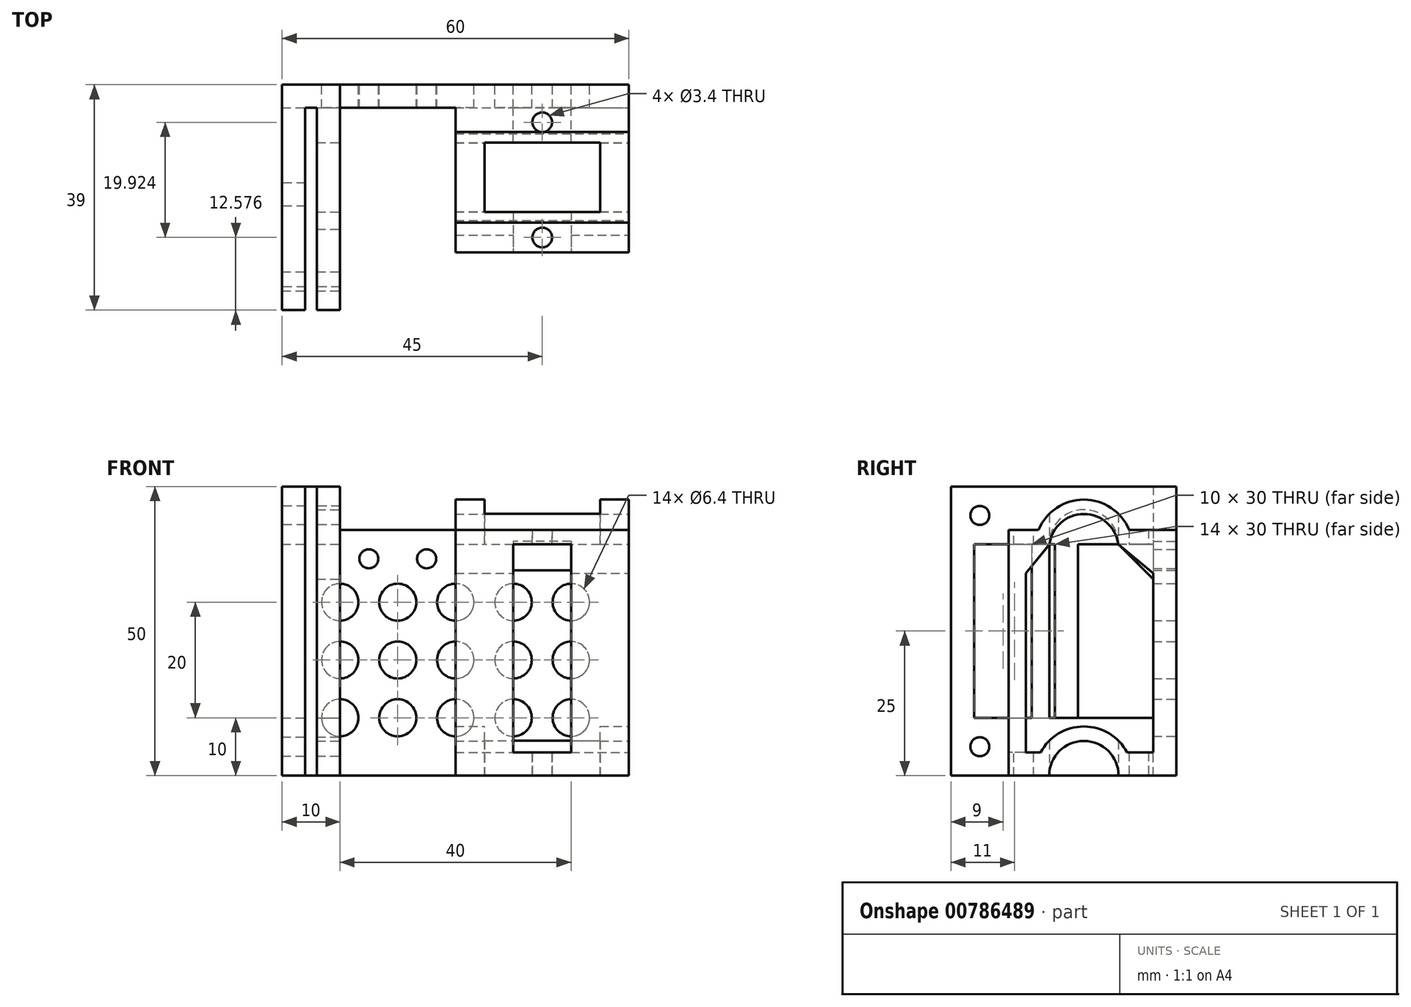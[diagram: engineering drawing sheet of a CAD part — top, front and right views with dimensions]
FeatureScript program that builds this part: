
annotation { "Feature Type Name" : "Feature", "Feature Type Description" : "" }
export const myFeature = defineFeature(function(context is Context, id is Id, definition is map)
    precondition{}
    {
        {
            var Q0;
            Q0=qCreatedBy(makeId("Front.planeOp"),FACE);
            var sketch = newSketch(context, id + "F0", { "sketchPlane" : qUnion([Q0])});
            skLineSegment(sketch, "E0.bottom", {"start": v(-30, 20) * mm, "end": v(30, 20) * mm});
            skLineSegment(sketch, "E0.top", {"start": v(-30, -20) * mm, "end": v(30, -20) * mm});
            skLineSegment(sketch, "E0.left", {"start": v(-30, 20) * mm, "end": v(-30, -20) * mm});
            skLineSegment(sketch, "E0.right", {"start": v(30, 20) * mm, "end": v(30, -20) * mm});
            skSolve(sketch);
        }
        {
            var Q0;
            Q0 = qSketchRegion(id + "F0", true);
            extrude(context, id + "F1", {"entities" : qUnion([Q0]), "depth" : 4 * mm, "offsetDistance" : 25 * mm});
        }
        {
            var Q0;
            Q0=makeQuery(id+"F1.opExtrude","CAP_FACE",FACE,{"disambiguationData":[OSD([sQuery(id+"F0.wireOp",EDGE,"E0.bottom"),sQuery(id+"F0.wireOp",EDGE,"E0.top"),sQuery(id+"F0.wireOp",EDGE,"E0.left"),sQuery(id+"F0.wireOp",EDGE,"E0.right")])],"isStart":false});
            var sketch = newSketch(context, id + "F2", { "sketchPlane" : qUnion([Q0])});
            skLineSegment(sketch, "E1.bottom", {"start": v(30, -20) * mm, "end": v(0, -20) * mm});
            skLineSegment(sketch, "E1.top", {"start": v(30, -10) * mm, "end": v(0, -10) * mm});
            skLineSegment(sketch, "E1.left", {"start": v(30, -20) * mm, "end": v(30, -10) * mm});
            skLineSegment(sketch, "E1.right", {"start": v(0, -20) * mm, "end": v(0, -10) * mm});
            skSolve(sketch);
        }
        {
            var Q0;
            Q0 = qSketchRegion(id + "F2", true);
            extrude(context, id + "F3", {"entities" : qUnion([Q0]), "operationType" : NewBodyOperationType.ADD, "depth" : 25 * mm, "offsetDistance" : 25 * mm});
        }
        {
            var Q0;
            Q0=makeQuery(id+"F1.opExtrude","CAP_FACE",FACE,{"disambiguationData":[OSD([sQuery(id+"F0.wireOp",EDGE,"E0.bottom"),sQuery(id+"F0.wireOp",EDGE,"E0.top"),sQuery(id+"F0.wireOp",EDGE,"E0.left"),sQuery(id+"F0.wireOp",EDGE,"E0.right")])],"isStart":false});
            var sketch = newSketch(context, id + "F4", { "sketchPlane" : qUnion([Q0])});
            skLineSegment(sketch, "E2.bottom", {"start": v(-30, -20) * mm, "end": v(-20, -20) * mm});
            skLineSegment(sketch, "E2.top", {"start": v(-30, -10) * mm, "end": v(-20, -10) * mm});
            skLineSegment(sketch, "E2.left", {"start": v(-30, -20) * mm, "end": v(-30, -10) * mm});
            skLineSegment(sketch, "E2.right", {"start": v(-20, -20) * mm, "end": v(-20, -10) * mm});
            skLineSegment(sketch, "E3.bottom", {"start": v(-17, -20) * mm, "end": v(-7, -20) * mm});
            skLineSegment(sketch, "E3.top", {"start": v(-17, 20) * mm, "end": v(-7, 20) * mm});
            skLineSegment(sketch, "E3.left", {"start": v(-17, -20) * mm, "end": v(-17, 20) * mm});
            skLineSegment(sketch, "E3.right", {"start": v(-7, -20) * mm, "end": v(-7, 20) * mm});
            skLineSegment(sketch, "E4.bottom", {"start": v(0, -15) * mm, "end": v(-4, -15) * mm});
            skLineSegment(sketch, "E4.top", {"start": v(0, -20) * mm, "end": v(-4, -20) * mm});
            skLineSegment(sketch, "E4.left", {"start": v(0, -15) * mm, "end": v(0, -20) * mm});
            skLineSegment(sketch, "E4.right", {"start": v(-4, -15) * mm, "end": v(-4, -20) * mm});
            skLineSegment(sketch, "E5.bottom", {"start": v(-26, -10) * mm, "end": v(-24, -10) * mm});
            skLineSegment(sketch, "E5.top", {"start": v(-26, -20) * mm, "end": v(-24, -20) * mm});
            skLineSegment(sketch, "E5.left", {"start": v(-26, -10) * mm, "end": v(-26, -20) * mm});
            skLineSegment(sketch, "E5.right", {"start": v(-24, -10) * mm, "end": v(-24, -20) * mm});
            skSolve(sketch);
        }
        {
            var Q0;
            {var subQ0=sQuery(id+"F4.wireOp",EDGE,"E2.left");Q0=makeQuery(id+"F4.imprint","IMPRINT",FACE,{"disambiguationData":[TD([[makeQuery(id+"F4.imprint","IMPRINT",EDGE,{"derivedFrom":subQ0}),1.0]])]});}
            var Q1;
            {var subQ0=sQuery(id+"F4.wireOp",EDGE,"E2.right");Q1=makeQuery(id+"F4.imprint","IMPRINT",FACE,{"disambiguationData":[TD([[makeQuery(id+"F4.imprint","IMPRINT",EDGE,{"derivedFrom":subQ0}),1.0]])]});}
            var Q2;
            Q2=makeQuery(id+"F4.imprint","IMPRINT",FACE,{"disambiguationData":[TD([[makeQuery(id+"F4.imprint","IMPRINT",EDGE,{"derivedFrom":sQuery(id+"F4.wireOp",EDGE,"E3.bottom")}),1.0]])]});
            extrude(context, id + "F5", {"entities" : qUnion([Q0, Q1, Q2]), "operationType" : NewBodyOperationType.ADD, "depth" : 25 * mm, "offsetDistance" : 25 * mm});
        }
        {
            var Q0;
            Q0=makeQuery(id+"F3.boolean.opBoolean","MERGE",FACE,{"derivedFrom":[makeQuery(id+"F1.opExtrude","SWEPT_FACE",FACE,{"disambiguationData":[OSD([sQuery(id+"F0.wireOp",EDGE,"E0.right")])]}),makeQuery(id+"F3.opExtrude","SWEPT_FACE",FACE,{"disambiguationData":[OSD([sQuery(id+"F2.wireOp",EDGE,"E1.left")])]})]});
            var sketch = newSketch(context, id + "F6", { "sketchPlane" : qUnion([Q0])});
            skCircle(sketch, "E6", {"center": v(-16.5, -20) * mm, "radius": 0.15 * mm});
            skLineSegment(sketch, "E7", {"start": v(-29, -10) * mm, "end": v(-16.5, -10) * mm});
            skSolve(sketch);
        }
        {
            var Q0;
            Q0=makeQuery(id+"F5.opExtrude","SWEPT_FACE",FACE,{"disambiguationData":[OSD([sQuery(id+"F4.wireOp",EDGE,"E2.right")])]});
            var sketch = newSketch(context, id + "F7", { "sketchPlane" : qUnion([Q0])});
            skCircle(sketch, "E8", {"center": v(-16, -20) * mm, "radius": 6 * mm});
            skSolve(sketch);
        }
        {
            var Q0;
            Q0 = qSketchRegion(id + "F7", true);
            extrude(context, id + "F8", {"entities" : qUnion([Q0]), "operationType" : NewBodyOperationType.REMOVE, "oppositeDirection" : true, "depth" : 4 * mm, "offsetDistance" : 25 * mm});
        }
        {
            var Q0;
            Q0=makeQuery(id+"F5.opExtrude","CAP_FACE",FACE,{"disambiguationData":[OSD([sQuery(id+"F4.wireOp",EDGE,"E2.bottom"),sQuery(id+"F4.wireOp",EDGE,"E2.top"),sQuery(id+"F4.wireOp",EDGE,"E2.right"),sQuery(id+"F4.wireOp",EDGE,"E5.right")])],"isStart":false});
            var sketch = newSketch(context, id + "F9", { "sketchPlane" : qUnion([Q0])});
            skLineSegment(sketch, "E9.bottom", {"start": v(-24, -10) * mm, "end": v(-20, -10) * mm});
            skLineSegment(sketch, "E9.top", {"start": v(-24, -20) * mm, "end": v(-20, -20) * mm});
            skLineSegment(sketch, "E9.left", {"start": v(-24, -10) * mm, "end": v(-24, -20) * mm});
            skLineSegment(sketch, "E9.right", {"start": v(-20, -10) * mm, "end": v(-20, -20) * mm});
            skSolve(sketch);
        }
        {
            var Q0;
            Q0 = qSketchRegion(id + "F9", true);
            extrude(context, id + "F10", {"entities" : qUnion([Q0]), "operationType" : NewBodyOperationType.ADD, "depth" : 10 * mm, "offsetDistance" : 25 * mm});
        }
        {
            var Q0;
            Q0=makeQuery(id+"F5.opExtrude","CAP_FACE",FACE,{"disambiguationData":[OSD([sQuery(id+"F4.wireOp",EDGE,"E2.bottom"),sQuery(id+"F4.wireOp",EDGE,"E2.top"),sQuery(id+"F4.wireOp",EDGE,"E2.left"),sQuery(id+"F4.wireOp",EDGE,"E5.left")])],"isStart":false});
            var sketch = newSketch(context, id + "F11", { "sketchPlane" : qUnion([Q0])});
            skLineSegment(sketch, "E10.bottom", {"start": v(-30, -10) * mm, "end": v(-26, -10) * mm});
            skLineSegment(sketch, "E10.top", {"start": v(-30, -20) * mm, "end": v(-26, -20) * mm});
            skLineSegment(sketch, "E10.left", {"start": v(-30, -10) * mm, "end": v(-30, -20) * mm});
            skLineSegment(sketch, "E10.right", {"start": v(-26, -10) * mm, "end": v(-26, -20) * mm});
            skSolve(sketch);
        }
        {
            var Q0;
            Q0 = qSketchRegion(id + "F11", true);
            extrude(context, id + "F12", {"entities" : qUnion([Q0]), "operationType" : NewBodyOperationType.ADD, "depth" : 10 * mm, "offsetDistance" : 25 * mm});
        }
        {
            var Q0;
            Q0=makeQuery(id+"F10.boolean.opBoolean","MERGE",FACE,{"derivedFrom":[makeQuery(id+"F5.opExtrude","SWEPT_FACE",FACE,{"disambiguationData":[OSD([sQuery(id+"F4.wireOp",EDGE,"E2.right")])]}),makeQuery(id+"F10.opExtrude","SWEPT_FACE",FACE,{"disambiguationData":[OSD([sQuery(id+"F9.wireOp",EDGE,"E9.right")])]})]});
            var sketch = newSketch(context, id + "F13", { "sketchPlane" : qUnion([Q0])});
            skCircle(sketch, "E11", {"center": v(-34, -15) * mm, "radius": 1.65 * mm});
            skPoint(sketch, "E11.centerSnap0", {"position": v(-39, -15) * mm});
            skSolve(sketch);
        }
        {
            var Q0;
            Q0 = qSketchRegion(id + "F13", true);
            extrude(context, id + "F14", {"entities" : qUnion([Q0]), "operationType" : NewBodyOperationType.REMOVE, "oppositeDirection" : true, "depth" : 25 * mm, "offsetDistance" : 25 * mm});
        }
        {
            var Q0;
            Q0=makeQuery(id+"F5.boolean.opBoolean","MERGE",FACE,{"derivedFrom":[makeQuery(id+"F1.opExtrude","SWEPT_FACE",FACE,{"disambiguationData":[OSD([sQuery(id+"F0.wireOp",EDGE,"E0.bottom")])]}),makeQuery(id+"F5.opExtrude","SWEPT_FACE",FACE,{"disambiguationData":[OSD([sQuery(id+"F4.wireOp",EDGE,"E3.top")])]})]});
            extrude(context, id + "F15", {"entities" : qUnion([Q0]), "operationType" : NewBodyOperationType.ADD, "depth" : 10 * mm, "offsetDistance" : 25 * mm});
        }
        {
            var Q0;
            {var subQ0=sQuery(id+"F7yCQw9h8FRDPHP_1.wireOp",EDGE,"DOwKe9Eh-Jl7f-Skud-Ed76-K8RTFp9YU4bL");var subQ1=sQuery(id+"F0.wireOp",EDGE,"E0.bottom");var subQ7=sQuery(id+"F0.wireOp",EDGE,"E0.top");var subQ14=sQuery(id+"F0.wireOp",EDGE,"E0.left");var subQ19=sQuery(id+"F0.wireOp",EDGE,"E0.right");var subQ20=makeQuery(id+"F1.opExtrude","CAP_FACE",FACE,{"disambiguationData":[OSD([subQ1,subQ7,subQ14,subQ19])],"isStart":false});Q0=makeQuery(id+"F15.boolean.opBoolean","MERGE",FACE,{"derivedFrom":[makeQuery(id+"FMx2agXSYsnFbtv_1.boolean.opBoolean","MERGE",FACE,{"derivedFrom":[makeQuery(id+"F5.boolean.opBoolean","SPLIT",FACE,{"disambiguationData":[TD([makeQuery(id+"F1.opExtrude","SWEPT_FACE",FACE,{"disambiguationData":[OSD([subQ19])]})])],"derivedFrom":subQ20}),makeQuery(id+"F5.boolean.opBoolean","SPLIT",FACE,{"disambiguationData":[TD([makeQuery(id+"F1.opExtrude","SWEPT_FACE",FACE,{"disambiguationData":[OSD([subQ14])]})])],"derivedFrom":subQ20}),makeQuery(id+"FMx2agXSYsnFbtv_1.opExtrude","SWEPT_FACE",FACE,{"disambiguationData":[OSD([subQ0])]})]}),makeQuery(id+"F15.opExtrude","SWEPT_FACE",FACE,{"disambiguationData":[OSD([subQ1,subQ0])]})]});}
            var sketch = newSketch(context, id + "F16", { "sketchPlane" : qUnion([Q0])});
            skLineSegment(sketch, "E12.bottom", {"start": v(-30, 30) * mm, "end": v(-26, 30) * mm});
            skLineSegment(sketch, "E12.top", {"start": v(-30, 20) * mm, "end": v(-26, 20) * mm});
            skLineSegment(sketch, "E12.left", {"start": v(-30, 30) * mm, "end": v(-30, 20) * mm});
            skLineSegment(sketch, "E12.right", {"start": v(-26, 30) * mm, "end": v(-26, 20) * mm});
            skLineSegment(sketch, "E13.bottom", {"start": v(-24, 30) * mm, "end": v(-20, 30) * mm});
            skLineSegment(sketch, "E13.top", {"start": v(-24, 20) * mm, "end": v(-20, 20) * mm});
            skLineSegment(sketch, "E13.left", {"start": v(-24, 30) * mm, "end": v(-24, 20) * mm});
            skLineSegment(sketch, "E13.right", {"start": v(-20, 30) * mm, "end": v(-20, 20) * mm});
            skSolve(sketch);
        }
        {
            var Q0;
            Q0 = qSketchRegion(id + "F16", true);
            extrude(context, id + "F17", {"entities" : qUnion([Q0]), "operationType" : NewBodyOperationType.ADD, "depth" : 35 * mm, "offsetDistance" : 25 * mm});
        }
        {
            var Q0;
            Q0=makeQuery(id+"F17.opExtrude","SWEPT_FACE",FACE,{"disambiguationData":[OSD([sQuery(id+"F16.wireOp",EDGE,"E13.right")])]});
            var sketch = newSketch(context, id + "F18", { "sketchPlane" : qUnion([Q0])});
            skCircle(sketch, "E14", {"center": v(-16, 20) * mm, "radius": 6 * mm});
            skSolve(sketch);
        }
        {
            var Q0;
            Q0 = qSketchRegion(id + "F18", true);
            extrude(context, id + "F19", {"entities" : qUnion([Q0]), "operationType" : NewBodyOperationType.REMOVE, "oppositeDirection" : true, "depth" : 4 * mm, "offsetDistance" : 25 * mm});
        }
        {
            var Q0;
            Q0 = qSketchRegion(id + "F7", true);
            extrude(context, id + "F20", {"entities" : qUnion([Q0]), "operationType" : NewBodyOperationType.REMOVE, "oppositeDirection" : true, "depth" : 4 * mm, "offsetDistance" : 25 * mm});
        }
        {
            var Q0;
            {var subQ0=sQuery(id+"F0.wireOp",EDGE,"E0.left");Q0=makeQuery(id+"F17.boolean.opBoolean","MERGE",FACE,{"derivedFrom":[makeQuery(id+"F15.boolean.opBoolean","MERGE",FACE,{"derivedFrom":[makeQuery(id+"F12.boolean.opBoolean","MERGE",FACE,{"derivedFrom":[makeQuery(id+"F5.boolean.opBoolean","MERGE",FACE,{"derivedFrom":[makeQuery(id+"F1.opExtrude","SWEPT_FACE",FACE,{"disambiguationData":[OSD([subQ0])]}),makeQuery(id+"F5.opExtrude","SWEPT_FACE",FACE,{"disambiguationData":[OSD([sQuery(id+"F4.wireOp",EDGE,"E2.left")])]})]}),makeQuery(id+"F12.opExtrude","SWEPT_FACE",FACE,{"disambiguationData":[OSD([sQuery(id+"F11.wireOp",EDGE,"E10.left")])]})]}),makeQuery(id+"F15.opExtrude","SWEPT_FACE",FACE,{"disambiguationData":[OSD([sQuery(id+"F0.wireOp",EDGE,"E0.bottom"),subQ0])]})]}),makeQuery(id+"F17.opExtrude","SWEPT_FACE",FACE,{"disambiguationData":[OSD([sQuery(id+"F16.wireOp",EDGE,"E12.left")])]})]});}
            var sketch = newSketch(context, id + "F21", { "sketchPlane" : qUnion([Q0])});
            skCircle(sketch, "E15", {"center": v(34, 25) * mm, "radius": 1.65 * mm});
            skSolve(sketch);
        }
        {
            var Q0;
            Q0 = qSketchRegion(id + "F21", true);
            extrude(context, id + "F22", {"entities" : qUnion([Q0]), "operationType" : NewBodyOperationType.REMOVE, "oppositeDirection" : true, "depth" : 10 * mm, "offsetDistance" : 25 * mm});
        }
        {
            var Q0;
            {var subQ0=sQuery(id+"F7yCQw9h8FRDPHP_1.wireOp",EDGE,"DOwKe9Eh-Jl7f-Skud-Ed76-K8RTFp9YU4bL");var subQ1=sQuery(id+"F0.wireOp",EDGE,"E0.bottom");var subQ7=sQuery(id+"F0.wireOp",EDGE,"E0.top");var subQ14=sQuery(id+"F0.wireOp",EDGE,"E0.left");var subQ19=sQuery(id+"F0.wireOp",EDGE,"E0.right");var subQ20=makeQuery(id+"F1.opExtrude","CAP_FACE",FACE,{"disambiguationData":[OSD([subQ1,subQ7,subQ14,subQ19])],"isStart":false});Q0=makeQuery(id+"F15.boolean.opBoolean","MERGE",FACE,{"derivedFrom":[makeQuery(id+"FMx2agXSYsnFbtv_1.boolean.opBoolean","MERGE",FACE,{"derivedFrom":[makeQuery(id+"F5.boolean.opBoolean","SPLIT",FACE,{"disambiguationData":[TD([makeQuery(id+"F1.opExtrude","SWEPT_FACE",FACE,{"disambiguationData":[OSD([subQ19])]})])],"derivedFrom":subQ20}),makeQuery(id+"F5.boolean.opBoolean","SPLIT",FACE,{"disambiguationData":[TD([makeQuery(id+"F1.opExtrude","SWEPT_FACE",FACE,{"disambiguationData":[OSD([subQ14])]})])],"derivedFrom":subQ20}),makeQuery(id+"FMx2agXSYsnFbtv_1.opExtrude","SWEPT_FACE",FACE,{"disambiguationData":[OSD([subQ0])]})]}),makeQuery(id+"F15.opExtrude","SWEPT_FACE",FACE,{"disambiguationData":[OSD([subQ1,subQ0])]})]});}
            var sketch = newSketch(context, id + "F23", { "sketchPlane" : qUnion([Q0])});
            skLineSegment(sketch, "E16.bottom", {"start": v(30, 30) * mm, "end": v(0, 30) * mm});
            skLineSegment(sketch, "E16.top", {"start": v(30, 20) * mm, "end": v(0, 20) * mm});
            skLineSegment(sketch, "E16.left", {"start": v(30, 30) * mm, "end": v(30, 20) * mm});
            skLineSegment(sketch, "E16.right", {"start": v(0, 30) * mm, "end": v(0, 20) * mm});
            skSolve(sketch);
        }
        {
            var Q0;
            Q0 = qSketchRegion(id + "F23", true);
            extrude(context, id + "F24", {"entities" : qUnion([Q0]), "operationType" : NewBodyOperationType.ADD, "depth" : 25 * mm, "offsetDistance" : 25 * mm});
        }
        {
            var Q0;
            {var subQ0=sQuery(id+"F4.wireOp",EDGE,"E2.top");Q0=makeQuery(id+"F12.boolean.opBoolean","MERGE",FACE,{"derivedFrom":[makeQuery(id+"F5.opExtrude","SWEPT_FACE",FACE,{"disambiguationData":[OSD([subQ0]),TDD([makeQuery(id+"F4.imprint","IMPRINT",EDGE,{"disambiguationData":[TD([[makeQuery(id+"F4.imprint","INTERSECT",VERTEX,{"derivedFrom":[subQ0,sQuery(id+"F4.wireOp",EDGE,"E5.left")]}),1.0]])],"derivedFrom":subQ0})])]}),makeQuery(id+"F12.opExtrude","SWEPT_FACE",FACE,{"disambiguationData":[OSD([sQuery(id+"F11.wireOp",EDGE,"E10.bottom")])]})]});}
            var sketch = newSketch(context, id + "F25", { "sketchPlane" : qUnion([Q0])});
            skLineSegment(sketch, "E17.bottom", {"start": v(-20, -39) * mm, "end": v(-24, -39) * mm});
            skLineSegment(sketch, "E17.top", {"start": v(-20, -35) * mm, "end": v(-24, -35) * mm});
            skLineSegment(sketch, "E17.left", {"start": v(-20, -39) * mm, "end": v(-20, -35) * mm});
            skLineSegment(sketch, "E17.right", {"start": v(-24, -39) * mm, "end": v(-24, -35) * mm});
            skLineSegment(sketch, "E18.bottom", {"start": v(-26, -39) * mm, "end": v(-30, -39) * mm});
            skLineSegment(sketch, "E18.top", {"start": v(-26, -35) * mm, "end": v(-30, -35) * mm});
            skLineSegment(sketch, "E18.left", {"start": v(-26, -39) * mm, "end": v(-26, -35) * mm});
            skLineSegment(sketch, "E18.right", {"start": v(-30, -39) * mm, "end": v(-30, -35) * mm});
            skSolve(sketch);
        }
        {
            var Q0;
            Q0 = qSketchRegion(id + "F25", true);
            extrude(context, id + "F26", {"entities" : qUnion([Q0]), "operationType" : NewBodyOperationType.ADD, "depth" : 30 * mm, "offsetDistance" : 25 * mm});
        }
        {
            var Q0;
            Q0=makeQuery(id+"F26.boolean.opBoolean","MERGE",FACE,{"derivedFrom":[makeQuery(id+"F10.boolean.opBoolean","MERGE",FACE,{"derivedFrom":[makeQuery(id+"F5.opExtrude","SWEPT_FACE",FACE,{"disambiguationData":[OSD([sQuery(id+"F4.wireOp",EDGE,"E2.right")])]}),makeQuery(id+"F10.opExtrude","SWEPT_FACE",FACE,{"disambiguationData":[OSD([sQuery(id+"F9.wireOp",EDGE,"E9.right")])]})]}),makeQuery(id+"F17.opExtrude","SWEPT_FACE",FACE,{"disambiguationData":[OSD([sQuery(id+"F16.wireOp",EDGE,"E13.right")])]}),makeQuery(id+"F26.opExtrude","SWEPT_FACE",FACE,{"disambiguationData":[OSD([sQuery(id+"F25.wireOp",EDGE,"E17.left")])]})]});
            var sketch = newSketch(context, id + "F27", { "sketchPlane" : qUnion([Q0])});
            skLineSegment(sketch, "E19.bottom", {"start": v(-22, 20) * mm, "end": v(-25, 20) * mm});
            skLineSegment(sketch, "E19.top", {"start": v(-22, -10) * mm, "end": v(-25, -10) * mm});
            skLineSegment(sketch, "E19.left", {"start": v(-22, 20) * mm, "end": v(-22, -10) * mm});
            skLineSegment(sketch, "E19.right", {"start": v(-25, 20) * mm, "end": v(-25, -10) * mm});
            skLineSegment(sketch, "E20", {"start": v(-10, 20) * mm, "end": v(-4, 14) * mm});
            skLineSegment(sketch, "E21", {"start": v(-10, 20) * mm, "end": v(-4, 20) * mm});
            skLineSegment(sketch, "E22", {"start": v(-4, 20) * mm, "end": v(-4, 14) * mm});
            skSolve(sketch);
        }
        {
            var Q0;
            Q0 = qSketchRegion(id + "F27", true);
            extrude(context, id + "F28", {"entities" : qUnion([Q0]), "operationType" : NewBodyOperationType.ADD, "oppositeDirection" : true, "depth" : 4 * mm, "offsetDistance" : 25 * mm});
        }
        {
            var Q0;
            {var subQ0=sQuery(id+"F0.wireOp",EDGE,"E0.left");Q0=makeQuery(id+"F26.boolean.opBoolean","MERGE",FACE,{"derivedFrom":[makeQuery(id+"F17.boolean.opBoolean","MERGE",FACE,{"derivedFrom":[makeQuery(id+"F15.boolean.opBoolean","MERGE",FACE,{"derivedFrom":[makeQuery(id+"F12.boolean.opBoolean","MERGE",FACE,{"derivedFrom":[makeQuery(id+"F5.boolean.opBoolean","MERGE",FACE,{"derivedFrom":[makeQuery(id+"F1.opExtrude","SWEPT_FACE",FACE,{"disambiguationData":[OSD([subQ0])]}),makeQuery(id+"F5.opExtrude","SWEPT_FACE",FACE,{"disambiguationData":[OSD([sQuery(id+"F4.wireOp",EDGE,"E2.left")])]})]}),makeQuery(id+"F12.opExtrude","SWEPT_FACE",FACE,{"disambiguationData":[OSD([sQuery(id+"F11.wireOp",EDGE,"E10.left")])]})]}),makeQuery(id+"F15.opExtrude","SWEPT_FACE",FACE,{"disambiguationData":[OSD([sQuery(id+"F0.wireOp",EDGE,"E0.bottom"),subQ0])]})]}),makeQuery(id+"F17.opExtrude","SWEPT_FACE",FACE,{"disambiguationData":[OSD([sQuery(id+"F16.wireOp",EDGE,"E12.left")])]})]}),makeQuery(id+"F26.opExtrude","SWEPT_FACE",FACE,{"disambiguationData":[OSD([sQuery(id+"F25.wireOp",EDGE,"E18.right")])]})]});}
            var sketch = newSketch(context, id + "F29", { "sketchPlane" : qUnion([Q0])});
            skLineSegment(sketch, "E23.bottom", {"start": v(17, 20) * mm, "end": v(21, 20) * mm});
            skLineSegment(sketch, "E23.top", {"start": v(17, -10) * mm, "end": v(21, -10) * mm});
            skLineSegment(sketch, "E23.left", {"start": v(17, 20) * mm, "end": v(17, -10) * mm});
            skLineSegment(sketch, "E23.right", {"start": v(21, 20) * mm, "end": v(21, -10) * mm});
            skSolve(sketch);
        }
        {
            var Q0;
            Q0 = qSketchRegion(id + "F29", true);
            extrude(context, id + "F30", {"entities" : qUnion([Q0]), "operationType" : NewBodyOperationType.ADD, "oppositeDirection" : true, "depth" : 4 * mm, "offsetDistance" : 25 * mm});
        }
        {
            var Q0;
            Q0=makeQuery(id+"F3.opExtrude","SWEPT_FACE",FACE,{"disambiguationData":[OSD([sQuery(id+"F2.wireOp",EDGE,"E1.top")])]});
            var sketch = newSketch(context, id + "F31", { "sketchPlane" : qUnion([Q0])});
            skLineSegment(sketch, "E24.bottom", {"start": v(0, -29) * mm, "end": v(30, -29) * mm});
            skLineSegment(sketch, "E24.top", {"start": v(0, -26) * mm, "end": v(30, -26) * mm});
            skLineSegment(sketch, "E24.left", {"start": v(0, -29) * mm, "end": v(0, -26) * mm});
            skLineSegment(sketch, "E24.right", {"start": v(30, -29) * mm, "end": v(30, -26) * mm});
            skSolve(sketch);
        }
        {
            var Q0;
            Q0 = qSketchRegion(id + "F31", true);
            extrude(context, id + "F32", {"entities" : qUnion([Q0]), "operationType" : NewBodyOperationType.ADD, "depth" : 30 * mm, "offsetDistance" : 25 * mm});
        }
        {
            var Q0;
            {var subQ0=sQuery(id+"F0.wireOp",EDGE,"E0.right");Q0=makeQuery(id+"F32.boolean.opBoolean","MERGE",FACE,{"derivedFrom":[makeQuery(id+"F24.boolean.opBoolean","MERGE",FACE,{"derivedFrom":[makeQuery(id+"F15.boolean.opBoolean","MERGE",FACE,{"derivedFrom":[makeQuery(id+"FrBbq9cCnRRpS4j_1.boolean.opBoolean","MERGE",FACE,{"derivedFrom":[makeQuery(id+"F3.boolean.opBoolean","MERGE",FACE,{"derivedFrom":[makeQuery(id+"F1.opExtrude","SWEPT_FACE",FACE,{"disambiguationData":[OSD([subQ0])]}),makeQuery(id+"F3.opExtrude","SWEPT_FACE",FACE,{"disambiguationData":[OSD([sQuery(id+"F2.wireOp",EDGE,"E1.left")])]})]}),makeQuery(id+"FrBbq9cCnRRpS4j_1.opExtrude","CAP_FACE",FACE,{"disambiguationData":[OSD([sQuery(id+"F6.wireOp",EDGE,"E6")])],"isStart":true})]}),makeQuery(id+"F15.opExtrude","SWEPT_FACE",FACE,{"disambiguationData":[OSD([sQuery(id+"F0.wireOp",EDGE,"E0.bottom"),subQ0])]})]}),makeQuery(id+"F24.opExtrude","SWEPT_FACE",FACE,{"disambiguationData":[OSD([sQuery(id+"F23.wireOp",EDGE,"E16.left")])]})]}),makeQuery(id+"F32.opExtrude","SWEPT_FACE",FACE,{"disambiguationData":[OSD([sQuery(id+"F31.wireOp",EDGE,"E24.right")])]})]});}
            var sketch = newSketch(context, id + "F33", { "sketchPlane" : qUnion([Q0])});
            skArc(sketch, "E25", {"start": v(-10.05, 20) * mm, "mid": v(-16, 25.24) * mm, "end": v(-21.95, 20) * mm});
            skArc(sketch, "E26", {"start": v(-7.53, 20) * mm, "mid": v(-16, 27.74) * mm, "end": v(-24.47, 20) * mm});
            skArc(sketch, "E27", {"start": v(-10, -20) * mm, "mid": v(-16, -14) * mm, "end": v(-22, -20) * mm});
            skArc(sketch, "E28", {"start": v(-7.5, -20) * mm, "mid": v(-16, -11.5) * mm, "end": v(-24.5, -20) * mm});
            skLineSegment(sketch, "E29", {"start": v(-22, -20) * mm, "end": v(-24.5, -20) * mm});
            skLineSegment(sketch, "E30", {"start": v(-10, -20) * mm, "end": v(-7.5, -20) * mm});
            skLineSegment(sketch, "E31", {"start": v(-24.47, 20) * mm, "end": v(-21.95, 20) * mm});
            skLineSegment(sketch, "E32", {"start": v(-10.05, 20) * mm, "end": v(-7.53, 20) * mm});
            skLineSegment(sketch, "E33", {"start": v(-29, 22.5) * mm, "end": v(-29, 30) * mm});
            skLineSegment(sketch, "E34", {"start": v(-29, 30) * mm, "end": v(-4.99, 30) * mm});
            skLineSegment(sketch, "E35", {"start": v(-23.85, 22.5) * mm, "end": v(-29, 22.5) * mm});
            skPoint(sketch, "E36.orphan", {"position": v(-29, 20) * mm});
            skLineSegment(sketch, "E37", {"start": v(-8.15, 22.5) * mm, "end": v(-4, 22.5) * mm});
            skLineSegment(sketch, "E38", {"start": v(-4, 22.5) * mm, "end": v(-4, 30) * mm});
            skLineSegment(sketch, "E39", {"start": v(-4, 30) * mm, "end": v(-4.99, 30) * mm});
            skLineSegment(sketch, "E40", {"start": v(-26, -10) * mm, "end": v(-26, -16) * mm});
            skLineSegment(sketch, "E41", {"start": v(-26, -16) * mm, "end": v(-23.5, -16) * mm});
            skLineSegment(sketch, "E42", {"start": v(-4, -10) * mm, "end": v(-4, -16) * mm});
            skLineSegment(sketch, "E43", {"start": v(-4, -16) * mm, "end": v(-8.5, -16) * mm});
            skSolve(sketch);
        }
        {
            var Q0;
            {var subQ0=sQuery(id+"F33.wireOp",EDGE,"E25");Q0=makeQuery(id+"F33.imprint","IMPRINT",FACE,{"disambiguationData":[TD([[makeQuery(id+"F33.imprint","IMPRINT",EDGE,{"derivedFrom":subQ0}),1.0]])]});}
            var Q1;
            {var subQ0=sQuery(id+"F33.wireOp",EDGE,"E27");Q1=makeQuery(id+"F33.imprint","IMPRINT",FACE,{"disambiguationData":[TD([[makeQuery(id+"F33.imprint","IMPRINT",EDGE,{"derivedFrom":subQ0}),1.0]])]});}
            extrude(context, id + "F34", {"entities" : qUnion([Q0, Q1]), "operationType" : NewBodyOperationType.REMOVE, "oppositeDirection" : true, "depth" : 30 * mm, "offsetDistance" : 25 * mm});
        }
        {
            var Q0;
            {var subQ0=sQuery(id+"F0.wireOp",EDGE,"E0.right");Q0=makeQuery(id+"F32.boolean.opBoolean","MERGE",FACE,{"derivedFrom":[makeQuery(id+"F24.boolean.opBoolean","MERGE",FACE,{"derivedFrom":[makeQuery(id+"F15.boolean.opBoolean","MERGE",FACE,{"derivedFrom":[makeQuery(id+"FrBbq9cCnRRpS4j_1.boolean.opBoolean","MERGE",FACE,{"derivedFrom":[makeQuery(id+"F3.boolean.opBoolean","MERGE",FACE,{"derivedFrom":[makeQuery(id+"F1.opExtrude","SWEPT_FACE",FACE,{"disambiguationData":[OSD([subQ0])]}),makeQuery(id+"F3.opExtrude","SWEPT_FACE",FACE,{"disambiguationData":[OSD([sQuery(id+"F2.wireOp",EDGE,"E1.left")])]})]}),makeQuery(id+"FrBbq9cCnRRpS4j_1.opExtrude","CAP_FACE",FACE,{"disambiguationData":[OSD([sQuery(id+"F6.wireOp",EDGE,"E6")])],"isStart":true})]}),makeQuery(id+"F15.opExtrude","SWEPT_FACE",FACE,{"disambiguationData":[OSD([sQuery(id+"F0.wireOp",EDGE,"E0.bottom"),subQ0])]})]}),makeQuery(id+"F24.opExtrude","SWEPT_FACE",FACE,{"disambiguationData":[OSD([sQuery(id+"F23.wireOp",EDGE,"E16.left")])]})]}),makeQuery(id+"F32.opExtrude","SWEPT_FACE",FACE,{"disambiguationData":[OSD([sQuery(id+"F31.wireOp",EDGE,"E24.right")])]})]});}
            var sketch = newSketch(context, id + "F35", { "sketchPlane" : qUnion([Q0])});
            skLineSegment(sketch, "E44", {"start": v(-21.95, 20) * mm, "end": v(-26, 15) * mm});
            skLineSegment(sketch, "E45", {"start": v(-21.95, 20) * mm, "end": v(-26, 20) * mm});
            skLineSegment(sketch, "E46", {"start": v(-26, 20) * mm, "end": v(-26, 15) * mm});
            skLineSegment(sketch, "E47", {"start": v(-10.05, 20) * mm, "end": v(-4, 15) * mm});
            skLineSegment(sketch, "E48", {"start": v(-4, 15) * mm, "end": v(-4, 20) * mm});
            skLineSegment(sketch, "E49", {"start": v(-4, 20) * mm, "end": v(-10.05, 20) * mm});
            skSolve(sketch);
        }
        {
            var Q0;
            Q0=makeQuery(id+"F35.imprint","IMPRINT",FACE,{"disambiguationData":[TD([[makeQuery(id+"F35.imprint","IMPRINT",EDGE,{"derivedFrom":sQuery(id+"F35.wireOp",EDGE,"E47")}),1.0]])]});
            var Q1;
            Q1=makeQuery(id+"F35.imprint","IMPRINT",FACE,{"disambiguationData":[TD([[makeQuery(id+"F35.imprint","IMPRINT",EDGE,{"derivedFrom":sQuery(id+"F35.wireOp",EDGE,"E44")}),-1.0]])]});
            extrude(context, id + "F36", {"entities" : qUnion([Q0, Q1]), "operationType" : NewBodyOperationType.ADD, "oppositeDirection" : true, "depth" : 30 * mm, "offsetDistance" : 25 * mm});
        }
        {
            var Q0;
            Q0=makeQuery(id+"F32.boolean.opBoolean","MERGE",FACE,{"derivedFrom":[makeQuery(id+"F3.opExtrude","CAP_FACE",FACE,{"disambiguationData":[OSD([sQuery(id+"F2.wireOp",EDGE,"E1.bottom"),sQuery(id+"F2.wireOp",EDGE,"E1.top"),sQuery(id+"F2.wireOp",EDGE,"E1.left"),sQuery(id+"F2.wireOp",EDGE,"E1.right")])],"isStart":false}),makeQuery(id+"F24.opExtrude","CAP_FACE",FACE,{"disambiguationData":[OSD([sQuery(id+"F23.wireOp",EDGE,"E16.bottom"),sQuery(id+"F23.wireOp",EDGE,"E16.top"),sQuery(id+"F23.wireOp",EDGE,"E16.left"),sQuery(id+"F23.wireOp",EDGE,"E16.right")])],"isStart":false}),makeQuery(id+"F32.opExtrude","SWEPT_FACE",FACE,{"disambiguationData":[OSD([sQuery(id+"F31.wireOp",EDGE,"E24.bottom")])]})]});
            var sketch = newSketch(context, id + "F37", { "sketchPlane" : qUnion([Q0])});
            skLineSegment(sketch, "E50.bottom", {"start": v(10, 20) * mm, "end": v(20, 20) * mm});
            skLineSegment(sketch, "E50.top", {"start": v(10, 15) * mm, "end": v(20, 15) * mm});
            skLineSegment(sketch, "E50.left", {"start": v(10, 20) * mm, "end": v(10, 15) * mm});
            skLineSegment(sketch, "E50.right", {"start": v(20, 20) * mm, "end": v(20, 15) * mm});
            skSolve(sketch);
        }
        {
            var Q0;
            Q0 = qSketchRegion(id + "F37", true);
            extrude(context, id + "F38", {"entities" : qUnion([Q0]), "operationType" : NewBodyOperationType.REMOVE, "oppositeDirection" : true, "depth" : 25 * mm, "offsetDistance" : 25 * mm});
        }
        {
            var Q0;
            Q0=makeQuery(id+"F33.imprint","IMPRINT",FACE,{"disambiguationData":[TD([[makeQuery(id+"F33.imprint","IMPRINT",EDGE,{"derivedFrom":sQuery(id+"F33.wireOp",EDGE,"E33")}),1.0]])]});
            extrude(context, id + "F39", {"entities" : qUnion([Q0]), "operationType" : NewBodyOperationType.REMOVE, "oppositeDirection" : true, "depth" : 30 * mm, "offsetDistance" : 25 * mm});
        }
        {
            var Q0;
            {var subQ0=sQuery(id+"F0.wireOp",EDGE,"E0.right");Q0=makeQuery(id+"F36.boolean.opBoolean","MERGE",FACE,{"derivedFrom":[makeQuery(id+"F32.boolean.opBoolean","MERGE",FACE,{"derivedFrom":[makeQuery(id+"F24.boolean.opBoolean","MERGE",FACE,{"derivedFrom":[makeQuery(id+"F15.boolean.opBoolean","MERGE",FACE,{"derivedFrom":[makeQuery(id+"FrBbq9cCnRRpS4j_1.boolean.opBoolean","MERGE",FACE,{"derivedFrom":[makeQuery(id+"F3.boolean.opBoolean","MERGE",FACE,{"derivedFrom":[makeQuery(id+"F1.opExtrude","SWEPT_FACE",FACE,{"disambiguationData":[OSD([subQ0])]}),makeQuery(id+"F3.opExtrude","SWEPT_FACE",FACE,{"disambiguationData":[OSD([sQuery(id+"F2.wireOp",EDGE,"E1.left")])]})]}),makeQuery(id+"FrBbq9cCnRRpS4j_1.opExtrude","CAP_FACE",FACE,{"disambiguationData":[OSD([sQuery(id+"F6.wireOp",EDGE,"E6")])],"isStart":true})]}),makeQuery(id+"F15.opExtrude","SWEPT_FACE",FACE,{"disambiguationData":[OSD([sQuery(id+"F0.wireOp",EDGE,"E0.bottom"),subQ0])]})]}),makeQuery(id+"F24.opExtrude","SWEPT_FACE",FACE,{"disambiguationData":[OSD([sQuery(id+"F23.wireOp",EDGE,"E16.left")])]})]}),makeQuery(id+"F32.opExtrude","SWEPT_FACE",FACE,{"disambiguationData":[OSD([sQuery(id+"F31.wireOp",EDGE,"E24.right")])]})]}),makeQuery(id+"F36.opExtrude","CAP_FACE",FACE,{"disambiguationData":[OSD([sQuery(id+"F35.wireOp",EDGE,"E44"),sQuery(id+"F35.wireOp",EDGE,"E45"),sQuery(id+"F35.wireOp",EDGE,"E46")])],"isStart":true}),makeQuery(id+"F36.opExtrude","CAP_FACE",FACE,{"disambiguationData":[OSD([sQuery(id+"F35.wireOp",EDGE,"E47"),sQuery(id+"F35.wireOp",EDGE,"E48"),sQuery(id+"F35.wireOp",EDGE,"E49")])],"isStart":true})]});}
            var sketch = newSketch(context, id + "F40", { "sketchPlane" : qUnion([Q0])});
            skLineSegment(sketch, "E51.bottom", {"start": v(-4, 22.5) * mm, "end": v(0, 22.5) * mm});
            skLineSegment(sketch, "E51.top", {"start": v(-4, 30) * mm, "end": v(0, 30) * mm});
            skLineSegment(sketch, "E51.left", {"start": v(-4, 22.5) * mm, "end": v(-4, 30) * mm});
            skLineSegment(sketch, "E51.right", {"start": v(0, 22.5) * mm, "end": v(0, 30) * mm});
            skSolve(sketch);
        }
        {
            var Q0;
            Q0 = qSketchRegion(id + "F40", true);
            extrude(context, id + "F41", {"entities" : qUnion([Q0]), "operationType" : NewBodyOperationType.REMOVE, "oppositeDirection" : true, "depth" : 50 * mm, "offsetDistance" : 25 * mm});
        }
        {
            var Q0;
            Q0=makeQuery(id+"F33.imprint","IMPRINT",FACE,{"disambiguationData":[TD([[makeQuery(id+"F33.imprint","IMPRINT",EDGE,{"derivedFrom":sQuery(id+"F33.wireOp",EDGE,"E40")}),1.0]])]});
            extrude(context, id + "F42", {"entities" : qUnion([Q0]), "operationType" : NewBodyOperationType.REMOVE, "oppositeDirection" : true, "depth" : 30 * mm, "offsetDistance" : 25 * mm});
        }
        {
            var Q0;
            Q0=makeQuery(id+"F38.boolean.opBoolean","COPY",FACE,{"derivedFrom":makeQuery(id+"F38.opExtrude","SWEPT_FACE",FACE,{"disambiguationData":[OSD([sQuery(id+"F37.wireOp",EDGE,"E50.top")])]})});
            extrude(context, id + "F43", {"entities" : qUnion([Q0]), "operationType" : NewBodyOperationType.REMOVE, "oppositeDirection" : true, "depth" : 31 * mm, "offsetDistance" : 25 * mm});
        }
        {
            var Q0;
            {var subQ0=sQuery(id+"F0.wireOp",EDGE,"E0.bottom");Q0=makeQuery(id+"F15.boolean.opBoolean","MERGE",FACE,{"derivedFrom":[makeQuery(id+"F1.opExtrude","CAP_FACE",FACE,{"disambiguationData":[OSD([subQ0,sQuery(id+"F0.wireOp",EDGE,"E0.top"),sQuery(id+"F0.wireOp",EDGE,"E0.left"),sQuery(id+"F0.wireOp",EDGE,"E0.right")])],"isStart":true}),makeQuery(id+"F15.opExtrude","SWEPT_FACE",FACE,{"disambiguationData":[OSD([subQ0])]})]});}
            var sketch = newSketch(context, id + "F44", { "sketchPlane" : qUnion([Q0])});
            skCircle(sketch, "E52", {"center": v(-20, -10) * mm, "radius": 3.2 * mm});
            skCircle(sketch, "E53", {"center": v(-10, -10) * mm, "radius": 3.2 * mm});
            skCircle(sketch, "E54.MirrorC", {"center": v(-10, 10) * mm, "radius": 3.2 * mm});
            skCircle(sketch, "E55.MirrorC", {"center": v(-20, 10) * mm, "radius": 3.2 * mm});
            skCircle(sketch, "E56.MirrorC", {"center": v(10, 10) * mm, "radius": 3.2 * mm});
            skCircle(sketch, "E57.MirrorC", {"center": v(20, 10) * mm, "radius": 3.2 * mm});
            skCircle(sketch, "E58.MirrorC", {"center": v(10, -10) * mm, "radius": 3.2 * mm});
            skCircle(sketch, "E59.MirrorC", {"center": v(20, -10) * mm, "radius": 3.2 * mm});
            skCircle(sketch, "E60", {"center": v(0, 10) * mm, "radius": 3.2 * mm});
            skCircle(sketch, "E61.MirrorC", {"center": v(0, -10) * mm, "radius": 3.2 * mm});
            skCircle(sketch, "E62.MirrorC", {"center": v(10, 0) * mm, "radius": 3.2 * mm});
            skCircle(sketch, "E63.MirrorC", {"center": v(0, 0) * mm, "radius": 3.2 * mm});
            skCircle(sketch, "E64.MirrorC", {"center": v(-10, 0) * mm, "radius": 3.2 * mm});
            skCircle(sketch, "E65.MirrorC", {"center": v(-20, 0) * mm, "radius": 3.2 * mm});
            skCircle(sketch, "E66.MirrorC", {"center": v(20, 0) * mm, "radius": 3.2 * mm});
            skCircle(sketch, "E67", {"center": v(-15, 17.5) * mm, "radius": 1.65 * mm});
            skLineSegment(sketch, "E68", {"start": v(-10, 10) * mm, "end": v(-10, 0) * mm});
            skLineSegment(sketch, "E69", {"start": v(0, 10) * mm, "end": v(0, 0) * mm});
            skLineSegment(sketch, "E70", {"start": v(10, 10) * mm, "end": v(10, 0) * mm});
            skCircle(sketch, "E71.MirrorC", {"center": v(5, 17.5) * mm, "radius": 1.65 * mm});
            skCircle(sketch, "E72.MirrorC", {"center": v(15, 17.5) * mm, "radius": 1.65 * mm});
            skSolve(sketch);
        }
        {
            var Q0;
            Q0 = qSketchRegion(id + "F44", true);
            extrude(context, id + "F45", {"entities" : qUnion([Q0]), "operationType" : NewBodyOperationType.REMOVE, "oppositeDirection" : true, "depth" : 4 * mm, "offsetDistance" : 25 * mm});
        }
        {
            var Q0;
            {var subQ0=sQuery(id+"F4.wireOp",EDGE,"E5.right");var subQ1=sQuery(id+"F4.wireOp",EDGE,"E2.right");var subQ2=sQuery(id+"F4.wireOp",EDGE,"E2.top");var subQ3=sQuery(id+"F4.wireOp",EDGE,"E2.bottom");var subQ7=sQuery(id+"F4.wireOp",EDGE,"E3.bottom");var subQ8=sQuery(id+"F0.wireOp",EDGE,"E0.top");var subQ9=sQuery(id+"F4.wireOp",EDGE,"E2.left");var subQ11=sQuery(id+"F2.wireOp",EDGE,"E1.bottom");var subQ12=makeQuery(id+"F5.boolean.opBoolean","MERGE",FACE,{"derivedFrom":[makeQuery(id+"F3.boolean.opBoolean","MERGE",FACE,{"derivedFrom":[makeQuery(id+"F1.opExtrude","SWEPT_FACE",FACE,{"disambiguationData":[OSD([subQ8])]}),makeQuery(id+"F3.opExtrude","SWEPT_FACE",FACE,{"disambiguationData":[OSD([subQ11])]})]}),makeQuery(id+"F5.opExtrude","SWEPT_FACE",FACE,{"disambiguationData":[OSD([subQ3]),TDD([makeQuery(id+"F4.imprint","IMPRINT",EDGE,{"disambiguationData":[TD([[makeQuery(id+"F4.imprint","INTERSECT",VERTEX,{"derivedFrom":[subQ3,subQ9]}),-1.0]])],"derivedFrom":subQ3})])]}),makeQuery(id+"F5.opExtrude","SWEPT_FACE",FACE,{"disambiguationData":[OSD([subQ3]),TDD([makeQuery(id+"F4.imprint","IMPRINT",EDGE,{"disambiguationData":[TD([[makeQuery(id+"F4.imprint","INTERSECT",VERTEX,{"derivedFrom":[subQ3,subQ0]}),-1.0]])],"derivedFrom":subQ3})])]}),makeQuery(id+"F5.opExtrude","SWEPT_FACE",FACE,{"disambiguationData":[OSD([subQ7])]})]});var subQ17=sQuery(id+"F0.wireOp",EDGE,"E0.left");var subQ18=makeQuery(id+"F1.opExtrude","SWEPT_FACE",FACE,{"disambiguationData":[OSD([subQ17])]});var subQ38=sQuery(id+"F11.wireOp",EDGE,"E10.top");var subQ60=makeQuery(id+"F12.boolean.opBoolean","MERGE",FACE,{"derivedFrom":[makeQuery(id+"F8.boolean.opBoolean","SPLIT",FACE,{"disambiguationData":[TD([subQ18])],"derivedFrom":subQ12}),makeQuery(id+"F12.opExtrude","SWEPT_FACE",FACE,{"disambiguationData":[OSD([subQ38])]})]});Q0=qUnion([makeQuery(id+"F34.boolean.opBoolean","SPLIT",FACE,{"disambiguationData":[TD([makeQuery(id+"F32.opExtrude","SWEPT_FACE",FACE,{"disambiguationData":[OSD([sQuery(id+"F31.wireOp",EDGE,"E24.bottom")])]})])],"derivedFrom":subQ60}),makeQuery(id+"F34.boolean.opBoolean","SPLIT",FACE,{"disambiguationData":[TD([subQ18])],"derivedFrom":subQ60}),makeQuery(id+"F10.boolean.opBoolean","MERGE",FACE,{"derivedFrom":[makeQuery(id+"F8.boolean.opBoolean","SPLIT",FACE,{"disambiguationData":[TD([makeQuery(id+"F5.opExtrude","CAP_FACE",FACE,{"disambiguationData":[OSD([subQ3,subQ2,subQ1,subQ0])],"isStart":false})])],"derivedFrom":subQ12}),makeQuery(id+"F10.opExtrude","SWEPT_FACE",FACE,{"disambiguationData":[OSD([sQuery(id+"F9.wireOp",EDGE,"E9.top")])]})]})]);}
            var sketch = newSketch(context, id + "F46", { "sketchPlane" : qUnion([Q0])});
            skLineSegment(sketch, "E73.bottom", {"start": v(25, 22) * mm, "end": v(5, 22) * mm});
            skLineSegment(sketch, "E73.top", {"start": v(25, 10) * mm, "end": v(5, 10) * mm});
            skLineSegment(sketch, "E73.left", {"start": v(25, 22) * mm, "end": v(25, 10) * mm});
            skLineSegment(sketch, "E73.right", {"start": v(5, 22) * mm, "end": v(5, 10) * mm});
            skSolve(sketch);
        }
        {
            var Q0;
            Q0 = qSketchRegion(id + "F46", true);
            extrude(context, id + "F47", {"entities" : qUnion([Q0]), "operationType" : NewBodyOperationType.REMOVE, "oppositeDirection" : true, "depth" : 50 * mm, "offsetDistance" : 25 * mm});
        }
        {
            var Q0;
            {var subQ0=sQuery(id+"F4.wireOp",EDGE,"E3.top");Q0=makeQuery(id+"F15.boolean.opBoolean","MERGE",FACE,{"derivedFrom":[makeQuery(id+"F5.opExtrude","CAP_FACE",FACE,{"disambiguationData":[OSD([sQuery(id+"F4.wireOp",EDGE,"E3.bottom"),subQ0,sQuery(id+"F4.wireOp",EDGE,"E3.left"),sQuery(id+"F4.wireOp",EDGE,"E3.right")])],"isStart":false}),makeQuery(id+"F15.opExtrude","SWEPT_FACE",FACE,{"disambiguationData":[OSD([subQ0])]})]});}
            var sketch = newSketch(context, id + "F48", { "sketchPlane" : qUnion([Q0])});
            skSolve(sketch);
        }
        {
            var Q0;
            Q0=makeQuery(id+"F48.imprint","IMPRINT",FACE,{"disambiguationData":[TD([[makeQuery(id+"F48.imprint","IMPRINT",EDGE,{"derivedFrom":makeQuery(id+"F5.opExtrude","CAP_EDGE",EDGE,{"disambiguationData":[OSD([sQuery(id+"F4.wireOp",EDGE,"E3.bottom")])],"isStart":false})}),1.0]])]});
            extrude(context, id + "F49", {"entities" : qUnion([Q0]), "operationType" : NewBodyOperationType.REMOVE, "oppositeDirection" : true, "depth" : 25 * mm, "offsetDistance" : 25 * mm});
        }
        {
            var Q0;
            Q0=makeQuery(id+"F39.boolean.opBoolean","COPY",FACE,{"derivedFrom":makeQuery(id+"F39.opExtrude","SWEPT_FACE",FACE,{"disambiguationData":[OSD([sQuery(id+"F33.wireOp",EDGE,"E35")])]})});
            var sketch = newSketch(context, id + "F50", { "sketchPlane" : qUnion([Q0])});
            skCircle(sketch, "E74", {"center": v(15, -26.42) * mm, "radius": 1.7 * mm});
            skPoint(sketch, "E74.centerSnap0", {"position": v(15, -29) * mm});
            skPoint(sketch, "E74.centerSnap1", {"position": v(30, -26.42) * mm});
            skSolve(sketch);
        }
        {
            var Q0;
            Q0 = qSketchRegion(id + "F50", true);
            extrude(context, id + "F51", {"entities" : qUnion([Q0]), "operationType" : NewBodyOperationType.REMOVE, "oppositeDirection" : true, "depth" : 50 * mm, "offsetDistance" : 25 * mm});
        }
        {
            var Q0;
            {var subQ4=sQuery(id+"F0.wireOp",EDGE,"E0.left");var subQ5=makeQuery(id+"F1.opExtrude","SWEPT_FACE",FACE,{"disambiguationData":[OSD([subQ4])]});var subQ7=sQuery(id+"F0.wireOp",EDGE,"E0.top");var subQ10=sQuery(id+"F4.wireOp",EDGE,"E2.left");var subQ27=sQuery(id+"F11.wireOp",EDGE,"E10.top");var subQ36=sQuery(id+"F4.wireOp",EDGE,"E3.bottom");var subQ44=sQuery(id+"F4.wireOp",EDGE,"E5.right");var subQ47=sQuery(id+"F4.wireOp",EDGE,"E2.bottom");var subQ48=sQuery(id+"F2.wireOp",EDGE,"E1.bottom");Q0=makeQuery(id+"F34.boolean.opBoolean","SPLIT",FACE,{"disambiguationData":[TD([subQ5])],"derivedFrom":makeQuery(id+"F12.boolean.opBoolean","MERGE",FACE,{"derivedFrom":[makeQuery(id+"F8.boolean.opBoolean","SPLIT",FACE,{"disambiguationData":[TD([subQ5])],"derivedFrom":makeQuery(id+"F5.boolean.opBoolean","MERGE",FACE,{"derivedFrom":[makeQuery(id+"F3.boolean.opBoolean","MERGE",FACE,{"derivedFrom":[makeQuery(id+"F1.opExtrude","SWEPT_FACE",FACE,{"disambiguationData":[OSD([subQ7])]}),makeQuery(id+"F3.opExtrude","SWEPT_FACE",FACE,{"disambiguationData":[OSD([subQ48])]})]}),makeQuery(id+"F5.opExtrude","SWEPT_FACE",FACE,{"disambiguationData":[OSD([subQ47]),TDD([makeQuery(id+"F4.imprint","IMPRINT",EDGE,{"disambiguationData":[TD([[makeQuery(id+"F4.imprint","INTERSECT",VERTEX,{"derivedFrom":[subQ47,subQ10]}),-1.0]])],"derivedFrom":subQ47})])]}),makeQuery(id+"F5.opExtrude","SWEPT_FACE",FACE,{"disambiguationData":[OSD([subQ47]),TDD([makeQuery(id+"F4.imprint","IMPRINT",EDGE,{"disambiguationData":[TD([[makeQuery(id+"F4.imprint","INTERSECT",VERTEX,{"derivedFrom":[subQ47,subQ44]}),-1.0]])],"derivedFrom":subQ47})])]}),makeQuery(id+"F5.opExtrude","SWEPT_FACE",FACE,{"disambiguationData":[OSD([subQ36])]})]})}),makeQuery(id+"F12.opExtrude","SWEPT_FACE",FACE,{"disambiguationData":[OSD([subQ27])]})]})});}
            var sketch = newSketch(context, id + "F52", { "sketchPlane" : qUnion([Q0])});
            skCircle(sketch, "E75", {"center": v(15, 6.5) * mm, "radius": 1.7 * mm});
            skPoint(sketch, "E75.centerSnap0", {"position": v(15, 10) * mm});
            skSolve(sketch);
        }
        {
            var Q0;
            Q0 = qSketchRegion(id + "F52", true);
            extrude(context, id + "F53", {"entities" : qUnion([Q0]), "operationType" : NewBodyOperationType.REMOVE, "oppositeDirection" : true, "depth" : 50 * mm, "offsetDistance" : 25 * mm});
        }
        {
            var Q0;
            {var subQ0=sQuery(id+"F0.wireOp",EDGE,"E0.bottom");Q0=makeQuery(id+"F15.boolean.opBoolean","MERGE",FACE,{"derivedFrom":[makeQuery(id+"F1.opExtrude","CAP_FACE",FACE,{"disambiguationData":[OSD([subQ0,sQuery(id+"F0.wireOp",EDGE,"E0.top"),sQuery(id+"F0.wireOp",EDGE,"E0.left"),sQuery(id+"F0.wireOp",EDGE,"E0.right")])],"isStart":true}),makeQuery(id+"F15.opExtrude","SWEPT_FACE",FACE,{"disambiguationData":[OSD([subQ0]),TDD([makeQuery(id+"F1.opExtrude","CAP_EDGE",EDGE,{"disambiguationData":[OSD([subQ0])],"isStart":true})])]})]});}
            var sketch = newSketch(context, id + "F54", { "sketchPlane" : qUnion([Q0])});
            skLineSegment(sketch, "E76.bottom", {"start": v(-20, 20.5) * mm, "end": v(-10, 20.5) * mm});
            skLineSegment(sketch, "E76.top", {"start": v(-20, 15.5) * mm, "end": v(-10, 15.5) * mm});
            skLineSegment(sketch, "E76.left", {"start": v(-20, 20.5) * mm, "end": v(-20, 15.5) * mm});
            skLineSegment(sketch, "E76.right", {"start": v(-10, 20.5) * mm, "end": v(-10, 15.5) * mm});
            skSolve(sketch);
        }
        {
            var Q0;
            Q0 = qSketchRegion(id + "F54", true);
            extrude(context, id + "F55", {"entities" : qUnion([Q0]), "operationType" : NewBodyOperationType.REMOVE, "oppositeDirection" : true, "depth" : 4 * mm, "offsetDistance" : 25 * mm});
        }
    });
